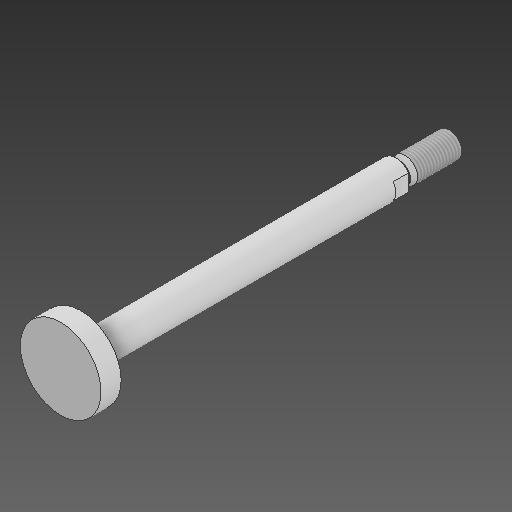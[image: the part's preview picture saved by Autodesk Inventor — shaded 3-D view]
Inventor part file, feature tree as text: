
AUTODESK INVENTOR PART (.ipt)
format: ipt  version: 2021 (Build 250183000, 183)  size: 161,792 bytes
history: native  units: in
note: dims shown in document units (in); Inventor stores cm internally (conversion verified against a paired STEP export)
features: other x31, sketch x3
ambient origin geometry x8: Origin, YZ Plane, XZ Plane, XY Plane, X Axis, Y Axis, Z Axis, Center Point
bodies: Solid1 (feature_tree)
feature tree (34):
  other  "193992 DSNU-32-60-PPS---(A---00--0-KS).ipt"
  other  "Solid1::193992 DSNU-32-60-PPS---(A---00--0-KS).ipt"
  other  "TaggingFeature1"
  sketch  "Sketch_2"  dims[d0=0.3937in]
  sketch  "Sketch_6"
  sketch  "Sketch_7"
  other  "FDT_KSAUFSATZ_XY"
  other  "FDT_KSAUFSATZ_YZ"
  other  "FDT_KSAUFSATZ_ZX"
  other  "FDT_NUT_XY"
  other  "FDT_NUT_YZ"
  other  "FDT_NUT_ZX"
  other  "KS_XY"
  other  "KS_YZ"
  other  "KS_ZX"
  other  "NUT1_XY"
  other  "NUT1_YZ"
  other  "NUT1_ZX"
  other  "FDT_KSAUFSATZ_X"
  other  "FDT_KSAUFSATZ_Y"
  other  "FDT_KSAUFSATZ_Z"
  other  "FDT_NUT_X"
  other  "FDT_NUT_Y"
  other  "FDT_NUT_Z"
  other  "KS_X"
  other  "KS_Y"
  other  "KS_Z"
  other  "NUT1_X"
  other  "NUT1_Y"
  other  "NUT1_Z"
  other  "FDT_KSAUFSATZ_Center"
  other  "FDT_NUT_Center"
  other  "KS_Center"
  other  "NUT1_Center"
